# Revit family: HB LED 150_200
name_source: partatom
category: Осветительные приборы
revit_build: Autodesk Revit 2016 (Build: 20161004_0715(x64)
units: mm (PartAtom-declared; Revit-internal decimal feet)

## family parameters
Источник света = Нет
Общий = Нет
Основа = Грань
При загрузке вырезать с полостями = Нет
Размер круглого соединителя = Использовать диаметр
Тип детали = Нормальный
Точка расчета площади = Нет

## types (1)
- HB LED 150_200
    ADSK_Единица измерения = Шт.
    ADSK_Завод-изготовитель = ООО МГК Световые технологии
    ADSK_Классификация нагрузок = Прочее
    ADSK_Код изделия = 1156000080
    ADSK_Количество фаз = 1
    ADSK_Количество фаз числовое = 1
    ADSK_Коэффициент мощности = 0.96
    ADSK_Масса = 7
    ADSK_Наименование = Второе поколение серии энергоэффективных модульных светильников для освещения промышленных цехов и логистических комплексов с потолками выше 8 метров. Главными достоинствами светильника являются высокая световая отдача – более 110 лм/Вт, и оригинальная система отведения тепла, обеспечивающая стабильность характеристик на протяжении всего срока службы. Для эксплуатации в тяжелых условиях и пожароопасных зонах возможна комплектация светильника прозрачным темперированным стеклом.
    ADSK_Напряжение = 230 В
    ADSK_Номинальная мощность = 0 кВт
    ADSK_Полная мощность = 0 кВ·А
    ADSK_Размер_Высота = 245 мм
    ADSK_Размер_Длина = 463 мм
    ADSK_Размер_Ширина = 249 мм
    ADSK_Ток = 1 А
    ADSK_Энергоэффективность = 111 лм/Вт
    IP Class = IP66
    URL = http://ltcompany.com
    Блок аварийного питания = Нет
    Выбор ИС = IES HB LED_150_200 : HB LED 150 D40 5000K
    Группа модели = Светильники
    Да = Нет
    Изготовитель = ООО МГК Световые технологии
    Излучатели = Плафон самосвечение
    Класс Защиты = II
    Класс пожароопасности = П-I,II,IIa,ІІІ
    Климатическая зона = УХЛ1
    Код по классификатору = D5020200
    Корпус = Металлик металл
    Нет = Нет
    Область использования = Промышленные предприятия, Складские объекты, Спортзалы, Транспортные узлы (вокзалы, аэропорты), ТРЦ
    Описание = Второе поколение серии энергоэффективных модульных светильников для освещения промышленных цехов и логистических комплексов с потолками выше 8 метров. Главными достоинствами светильника являются высокая световая отдача – более 110 лм/Вт, и оригинальная система отведения тепла, обеспечивающая стабильность характеристик на протяжении всего срока службы. Для эксплуатации в тяжелых условиях и пожароопасных зонах возможна комплектация светильника прозрачным темперированным стеклом.
    Отметка по умолчанию = 0 мм
    Плафон = Плафон прозрачный
    Полная установленная мощность = 0 кВ·А
    Тип ИС = LED
    Тип ПРА = Драйвер
    Тип продукции = Светильник

## geometry (parser evidence)
native form markers: Blend x2
no freeform markers — native parametric forms only
